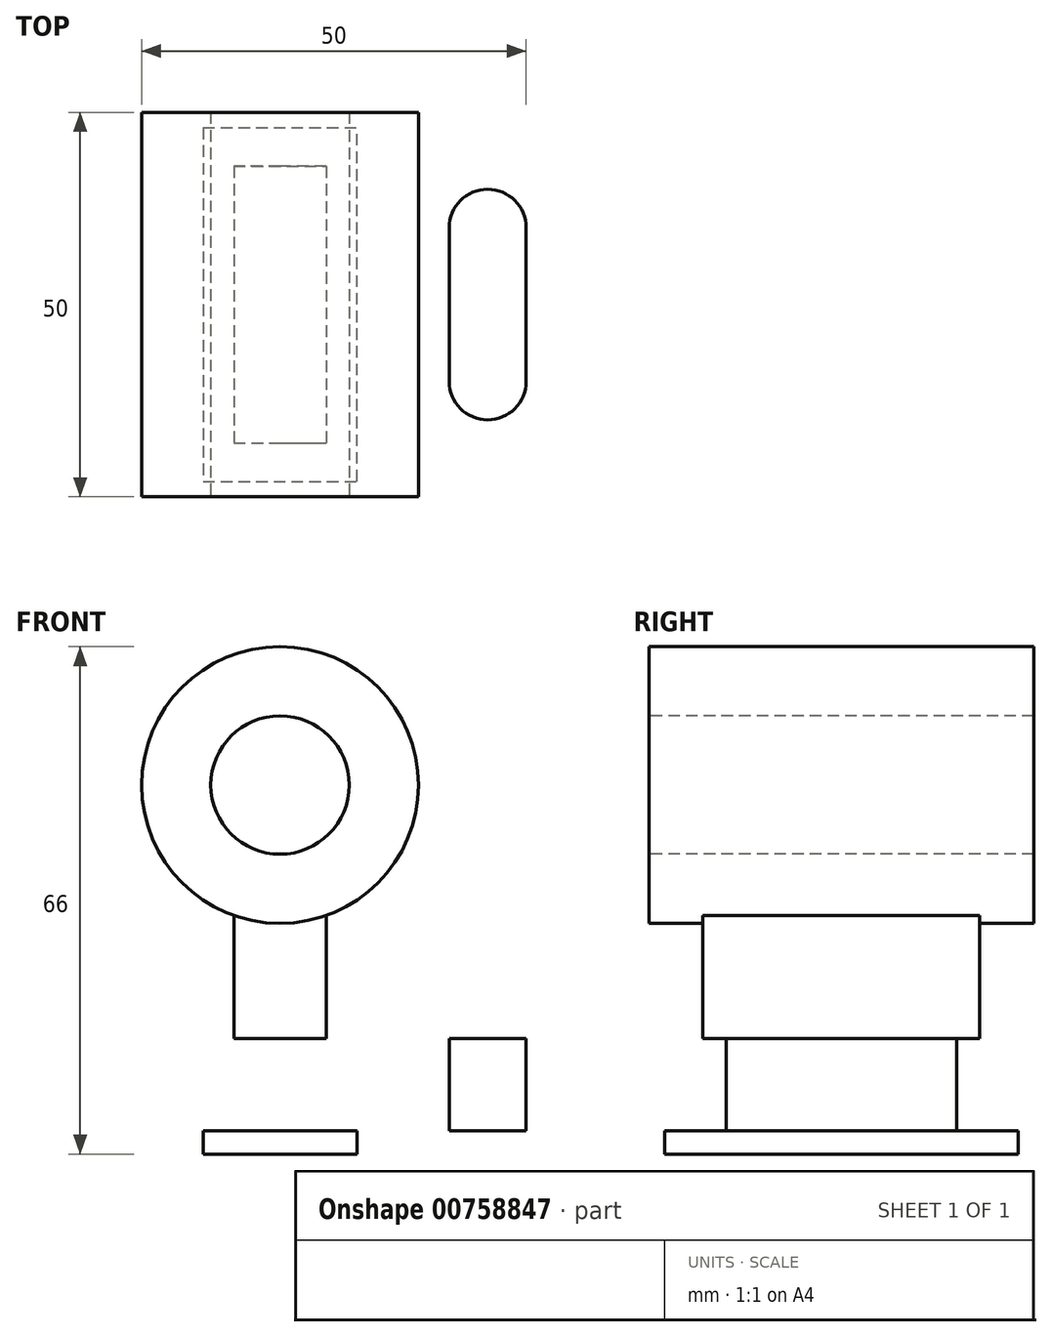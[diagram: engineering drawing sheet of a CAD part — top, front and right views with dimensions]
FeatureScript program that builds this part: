
annotation { "Feature Type Name" : "Feature", "Feature Type Description" : "" }
export const myFeature = defineFeature(function(context is Context, id is Id, definition is map)
    precondition{}
    {
        {
            var Q0;
            Q0=qCreatedBy(makeId("Top.planeOp"),FACE);
            var sketch = newSketch(context, id + "F0", { "sketchPlane" : qUnion([Q0])});
            skLineSegment(sketch, "E0.bottom", {"start": v(0, 0) * mm, "end": v(80, 0) * mm});
            skLineSegment(sketch, "E0.top", {"start": v(0, 46) * mm, "end": v(80, 46) * mm});
            skLineSegment(sketch, "E0.left", {"start": v(0, 0) * mm, "end": v(0, 46) * mm});
            skLineSegment(sketch, "E0.right", {"start": v(80, 0) * mm, "end": v(80, 46) * mm});
            skSolve(sketch);
        }
        {
            var Q0;
            Q0=makeQuery(id+"F0.imprint","IMPRINT",FACE,{"disambiguationData":[TD([[makeQuery(id+"F0.imprint","IMPRINT",EDGE,{"derivedFrom":sQuery(id+"F0.wireOp",EDGE,"E0.bottom")}),1.0]])]});
            extrude(context, id + "F1", {"entities" : qUnion([Q0]), "depth" : 12 * mm, "offsetDistance" : 25 * mm});
        }
        {
            var Q0;
            Q0=makeQuery(id+"F1.opExtrude","CAP_FACE",FACE,{"disambiguationData":[OSD([sQuery(id+"F0.wireOp",EDGE,"E0.bottom"),sQuery(id+"F0.wireOp",EDGE,"E0.top"),sQuery(id+"F0.wireOp",EDGE,"E0.left"),sQuery(id+"F0.wireOp",EDGE,"E0.right")])],"isStart":true});
            var sketch = newSketch(context, id + "F2", { "sketchPlane" : qUnion([Q0])});
            skLineSegment(sketch, "E1", {"start": v(40, -46) * mm, "end": v(50, -46) * mm});
            skLineSegment(sketch, "E2", {"start": v(40, -46) * mm, "end": v(30, -46) * mm});
            skLineSegment(sketch, "E3", {"start": v(30, -46) * mm, "end": v(30, 0) * mm});
            skLineSegment(sketch, "E4", {"start": v(30, 0) * mm, "end": v(50, 0) * mm});
            skLineSegment(sketch, "E5", {"start": v(50, 0) * mm, "end": v(50, -46) * mm});
            skSolve(sketch);
        }
        {
            var Q0;
            Q0=makeQuery(id+"F2.imprint","IMPRINT",FACE,{"disambiguationData":[TD([[makeQuery(id+"F2.imprint","IMPRINT",EDGE,{"derivedFrom":sQuery(id+"F2.wireOp",EDGE,"E1")}),1.0]])]});
            extrude(context, id + "F3", {"entities" : qUnion([Q0]), "operationType" : NewBodyOperationType.ADD, "depth" : 3 * mm, "offsetDistance" : 25 * mm});
        }
        {
            var Q0;
            Q0=makeQuery(id+"F1.opExtrude","CAP_FACE",FACE,{"disambiguationData":[OSD([sQuery(id+"F0.wireOp",EDGE,"E0.bottom"),sQuery(id+"F0.wireOp",EDGE,"E0.top"),sQuery(id+"F0.wireOp",EDGE,"E0.left"),sQuery(id+"F0.wireOp",EDGE,"E0.right")])],"isStart":false});
            var sketch = newSketch(context, id + "F4", { "sketchPlane" : qUnion([Q0])});
            skLineSegment(sketch, "E6", {"start": v(8, 13) * mm, "end": v(8, 33) * mm});
            skLineSegment(sketch, "E7", {"start": v(18, 13) * mm, "end": v(18, 33) * mm});
            skArc(sketch, "E8", {"start": v(18, 33) * mm, "mid": v(13, 38) * mm, "end": v(8, 33) * mm});
            skArc(sketch, "E9", {"start": v(8, 13) * mm, "mid": v(13, 8) * mm, "end": v(18, 13) * mm});
            skArc(sketch, "E10.MirrorCS", {"start": v(62, 33) * mm, "mid": v(67, 38) * mm, "end": v(72, 33) * mm});
            skLineSegment(sketch, "E11.MirrorCS", {"start": v(72, 13) * mm, "end": v(72, 33) * mm});
            skLineSegment(sketch, "E12.MirrorCS", {"start": v(62, 13) * mm, "end": v(62, 33) * mm});
            skArc(sketch, "E13.MirrorCS", {"start": v(72, 13) * mm, "mid": v(67, 8) * mm, "end": v(62, 13) * mm});
            skPoint(sketch, "E14.endSnap0", {"position": v(40, 0) * mm});
            skSolve(sketch);
        }
        {
            var Q0;
            Q0=makeQuery(id+"F4.imprint","IMPRINT",FACE,{"disambiguationData":[TD([[makeQuery(id+"F4.imprint","IMPRINT",EDGE,{"derivedFrom":sQuery(id+"F4.wireOp",EDGE,"E6")}),-1.0]])]});
            var Q1;
            Q1=makeQuery(id+"F4.imprint","IMPRINT",FACE,{"disambiguationData":[TD([[makeQuery(id+"F4.imprint","IMPRINT",EDGE,{"derivedFrom":sQuery(id+"F4.wireOp",EDGE,"E10.MirrorCS")}),-1.0]])]});
            extrude(context, id + "F5", {"entities" : qUnion([Q0, Q1]), "operationType" : NewBodyOperationType.REMOVE, "oppositeDirection" : true, "depth" : 12 * mm, "offsetDistance" : 25 * mm});
        }
        {
            var Q0;
            Q0=makeQuery(id+"F1.opExtrude","CAP_FACE",FACE,{"disambiguationData":[OSD([sQuery(id+"F0.wireOp",EDGE,"E0.bottom"),sQuery(id+"F0.wireOp",EDGE,"E0.top"),sQuery(id+"F0.wireOp",EDGE,"E0.left"),sQuery(id+"F0.wireOp",EDGE,"E0.right")])],"isStart":false});
            var sketch = newSketch(context, id + "F6", { "sketchPlane" : qUnion([Q0])});
            skLineSegment(sketch, "E15", {"start": v(22, 48) * mm, "end": v(22, -2) * mm});
            skLineSegment(sketch, "E16", {"start": v(22, -2) * mm, "end": v(58, -2) * mm});
            skLineSegment(sketch, "E17", {"start": v(58, -2) * mm, "end": v(58, 48) * mm});
            skLineSegment(sketch, "E18", {"start": v(22, 48) * mm, "end": v(58, 48) * mm});
            skSolve(sketch);
        }
        {
            var Q0;
            {var subQ0=sQuery(id+"F6.wireOp",EDGE,"E15");var subQ1=makeQuery(id+"F1.opExtrude","CAP_EDGE",EDGE,{"disambiguationData":[OSD([sQuery(id+"F0.wireOp",EDGE,"E0.top")])],"isStart":false});var subQ2=makeQuery(id+"F6.imprint","INTERSECT",VERTEX,{"derivedFrom":[subQ1,subQ0]});Q0=makeQuery(id+"F6.imprint","IMPRINT",FACE,{"disambiguationData":[TD([[makeQuery(id+"F6.imprint","IMPRINT",EDGE,{"disambiguationData":[TD([[subQ2,-1.0]])],"derivedFrom":subQ0}),1.0]])]});}
            var Q1;
            {var subQ0=sQuery(id+"F6.wireOp",EDGE,"E16");Q1=makeQuery(id+"F6.imprint","IMPRINT",FACE,{"disambiguationData":[TD([[makeQuery(id+"F6.imprint","IMPRINT",EDGE,{"derivedFrom":subQ0}),1.0]])]});}
            var Q2;
            {var subQ0=sQuery(id+"F6.wireOp",EDGE,"E18");Q2=makeQuery(id+"F6.imprint","IMPRINT",FACE,{"disambiguationData":[TD([[makeQuery(id+"F6.imprint","IMPRINT",EDGE,{"derivedFrom":subQ0}),-1.0]])]});}
            extrude(context, id + "F7", {"entities" : qUnion([Q0, Q1, Q2]), "operationType" : NewBodyOperationType.ADD, "depth" : 51 * mm, "offsetDistance" : 25 * mm});
        }
        {
            var Q0;
            Q0=makeQuery(id+"F7.opExtrude","SWEPT_FACE",FACE,{"disambiguationData":[OSD([sQuery(id+"F6.wireOp",EDGE,"E16")])]});
            var sketch = newSketch(context, id + "F8", { "sketchPlane" : qUnion([Q0])});
            skCircle(sketch, "E19", {"center": v(40, 45) * mm, "radius": 18 * mm});
            skLineSegment(sketch, "E20", {"start": v(40, 12) * mm, "end": v(46, 12) * mm});
            skLineSegment(sketch, "E21", {"start": v(46, 12) * mm, "end": v(46, 28.03) * mm});
            skLineSegment(sketch, "E22", {"start": v(40, 12) * mm, "end": v(34, 12) * mm});
            skLineSegment(sketch, "E23", {"start": v(34, 12) * mm, "end": v(34, 28.03) * mm});
            skLineSegment(sketch, "E24", {"start": v(22, 63) * mm, "end": v(58, 63) * mm});
            skLineSegment(sketch, "E25", {"start": v(58, 63) * mm, "end": v(58, 12) * mm});
            skLineSegment(sketch, "E26", {"start": v(58, 12) * mm, "end": v(46, 12) * mm});
            skLineSegment(sketch, "E27", {"start": v(34, 12) * mm, "end": v(22, 12) * mm});
            skLineSegment(sketch, "E28", {"start": v(22, 12) * mm, "end": v(22, 63) * mm});
            skCircle(sketch, "E29", {"center": v(40, 45) * mm, "radius": 9 * mm});
            skSolve(sketch);
        }
        {
            var Q0;
            {var subQ0=sQuery(id+"F8.wireOp",EDGE,"E24");var subQ1=sQuery(id+"F8.wireOp",EDGE,"E19");var subQ2=makeQuery(id+"F8.imprint","INTERSECT",VERTEX,{"derivedFrom":[subQ1,subQ0]});Q0=makeQuery(id+"F8.imprint","IMPRINT",FACE,{"disambiguationData":[TD([[makeQuery(id+"F8.imprint","IMPRINT",EDGE,{"disambiguationData":[TD([[subQ2,-1.0]])],"derivedFrom":subQ1}),-1.0]])]});}
            var Q1;
            {var subQ0=sQuery(id+"F8.wireOp",EDGE,"E24");var subQ1=sQuery(id+"F8.wireOp",EDGE,"E19");var subQ2=makeQuery(id+"F8.imprint","INTERSECT",VERTEX,{"derivedFrom":[subQ1,subQ0]});Q1=makeQuery(id+"F8.imprint","IMPRINT",FACE,{"disambiguationData":[TD([[makeQuery(id+"F8.imprint","IMPRINT",EDGE,{"disambiguationData":[TD([[subQ2,1.0]])],"derivedFrom":subQ1}),-1.0]])]});}
            var Q2;
            {var subQ0=sQuery(id+"F8.wireOp",EDGE,"E21");Q2=makeQuery(id+"F8.imprint","IMPRINT",FACE,{"disambiguationData":[TD([[makeQuery(id+"F8.imprint","IMPRINT",EDGE,{"derivedFrom":subQ0}),-1.0]])]});}
            var Q3;
            {var subQ0=sQuery(id+"F8.wireOp",EDGE,"E23");Q3=makeQuery(id+"F8.imprint","IMPRINT",FACE,{"disambiguationData":[TD([[makeQuery(id+"F8.imprint","IMPRINT",EDGE,{"derivedFrom":subQ0}),1.0]])]});}
            var Q4;
            Q4=makeQuery(id+"F8.imprint","IMPRINT",FACE,{"disambiguationData":[TD([[makeQuery(id+"F8.imprint","IMPRINT",EDGE,{"derivedFrom":sQuery(id+"F8.wireOp",EDGE,"E29")}),1.0]])]});
            extrude(context, id + "F9", {"entities" : qUnion([Q0, Q1, Q2, Q3, Q4]), "operationType" : NewBodyOperationType.REMOVE, "oppositeDirection" : true, "depth" : 51 * mm, "offsetDistance" : 25 * mm});
        }
        {
            var Q0;
            Q0=makeQuery(id+"F7.opExtrude","SWEPT_FACE",FACE,{"disambiguationData":[OSD([sQuery(id+"F6.wireOp",EDGE,"E16")])]});
            var sketch = newSketch(context, id + "F10", { "sketchPlane" : qUnion([Q0])});
            skLineSegment(sketch, "E30", {"start": v(46, 12) * mm, "end": v(46, 28.03) * mm});
            skLineSegment(sketch, "E31", {"start": v(34, 12) * mm, "end": v(34, 28.03) * mm});
            skArc(sketch, "E32", {"start": v(34, 28.03) * mm, "mid": v(40, 27) * mm, "end": v(46, 28.03) * mm});
            skSolve(sketch);
        }
        {
            var Q0;
            Q0=makeQuery(id+"F10.imprint","IMPRINT",FACE,{"disambiguationData":[TD([[makeQuery(id+"F10.imprint","IMPRINT",EDGE,{"derivedFrom":sQuery(id+"F10.wireOp",EDGE,"E30")}),1.0]])]});
            extrude(context, id + "F11", {"entities" : qUnion([Q0]), "operationType" : NewBodyOperationType.REMOVE, "oppositeDirection" : true, "depth" : 7 * mm, "offsetDistance" : 25 * mm});
        }
        {
            var Q0;
            Q0=makeQuery(id+"F7.opExtrude","SWEPT_FACE",FACE,{"disambiguationData":[OSD([sQuery(id+"F6.wireOp",EDGE,"E18")])]});
            var sketch = newSketch(context, id + "F12", { "sketchPlane" : qUnion([Q0])});
            skLineSegment(sketch, "E33", {"start": v(-46, 12) * mm, "end": v(-46, 28.03) * mm});
            skLineSegment(sketch, "E34", {"start": v(-34, 28.03) * mm, "end": v(-34, 12) * mm});
            skArc(sketch, "E35", {"start": v(-46, 28.03) * mm, "mid": v(-40, 27) * mm, "end": v(-34, 28.03) * mm});
            skLineSegment(sketch, "E36", {"start": v(-46, 12) * mm, "end": v(-34, 12) * mm});
            skSolve(sketch);
        }
        {
            var Q0;
            Q0=makeQuery(id+"F12.imprint","IMPRINT",FACE,{"disambiguationData":[TD([[makeQuery(id+"F12.imprint","IMPRINT",EDGE,{"derivedFrom":sQuery(id+"F12.wireOp",EDGE,"E33")}),1.0]])]});
            extrude(context, id + "F13", {"entities" : qUnion([Q0]), "operationType" : NewBodyOperationType.REMOVE, "oppositeDirection" : true, "depth" : 7 * mm, "offsetDistance" : 25 * mm});
        }
    });
